# Revit family: DIN-Kreuzverbinder für Flachleiter, mit Zwischenplatte V4A
name_source: partatom
category: Generic Models
revit_build: Autodesk Revit 2015 (Build: 20140606_1530(x64)
units: mm (PartAtom-declared; Revit-internal decimal feet)

## types (1)
- 256 DIN 30 V4A
    Article Type = 256 DIN 30 V4A
    GTIN = 4012195893097
    Height = 3 mm  [stored 0.00984252 ft]
    Height 1 = 6 mm  [stored 0.019685 ft]
    Length = 60 mm  [stored 0.19685 ft]
    Length 1 = 20 mm  [stored 0.0656168 ft]
    Length 2 = 14 mm  [stored 0.0459318 ft]
    Manufacturer = OBO Bettermann
    Manufacturer Art.No. = 5314616
    Material = Stainless Steel
    URL = http://www.obo-bettermann.com
    Width = 60 mm  [stored 0.19685 ft]
    Width 1 = 20 mm  [stored 0.0656168 ft]
    Width 2 = 13 mm

note: [stored X ft] marks values corroborated as IEEE doubles in the binary element streams (Revit-internal decimal feet)

## geometry (parser evidence)
native form markers: Sweep x2
no freeform markers — native parametric forms only
